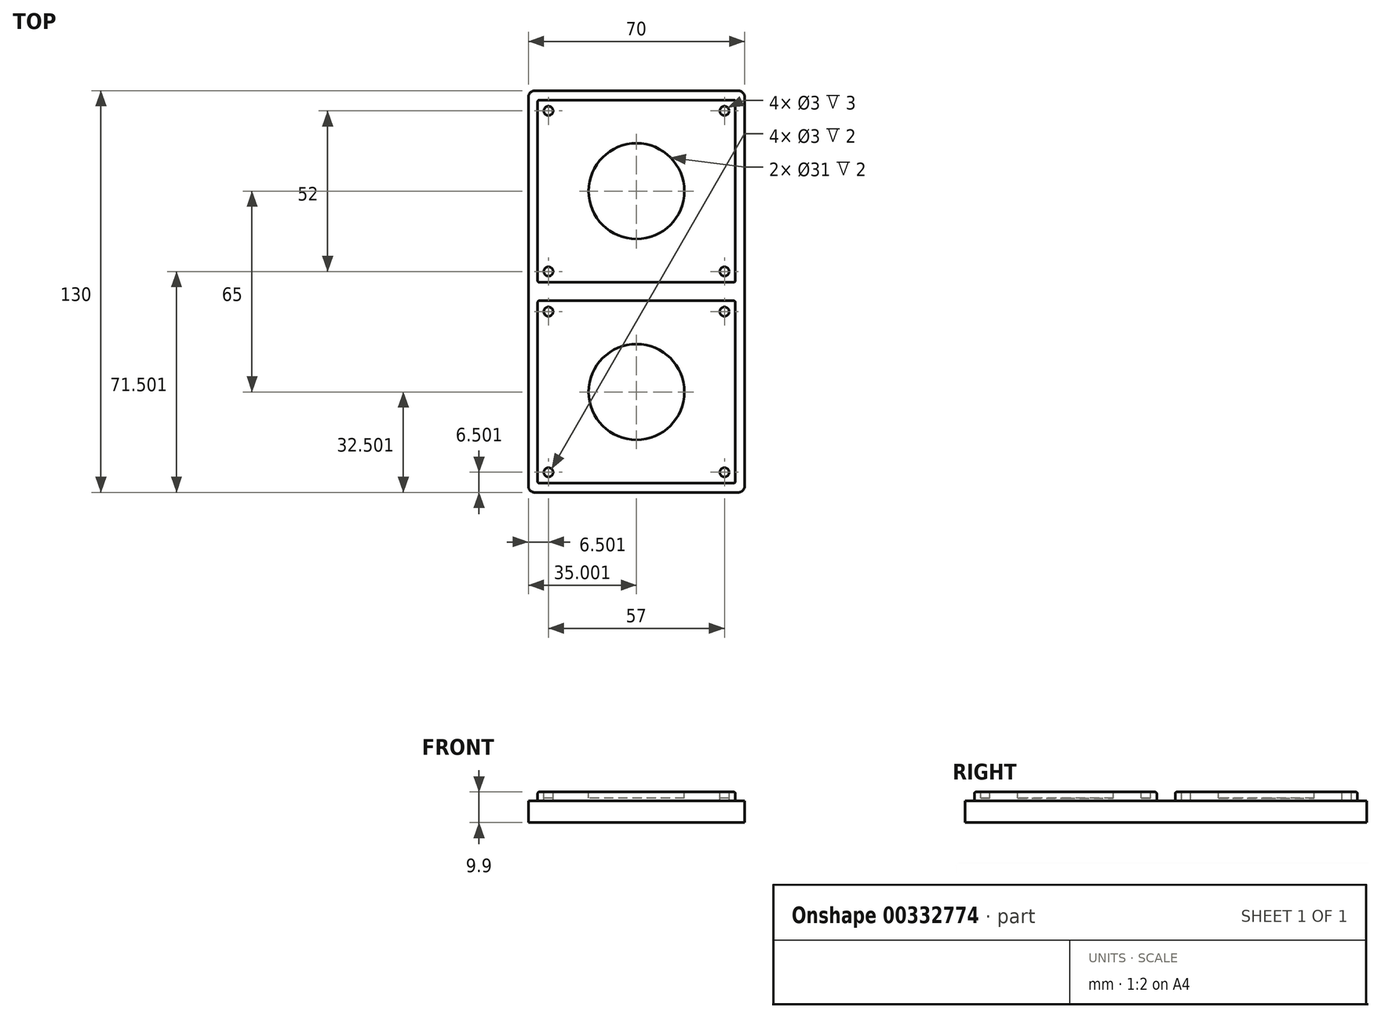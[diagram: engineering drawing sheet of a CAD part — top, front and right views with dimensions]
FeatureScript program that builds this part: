
annotation { "Feature Type Name" : "Feature", "Feature Type Description" : "" }
export const myFeature = defineFeature(function(context is Context, id is Id, definition is map)
    precondition{}
    {
        {
            var Q0;
            Q0=qCreatedBy(makeId("Top.planeOp"),FACE);
            var sketch = newSketch(context, id + "F0", { "sketchPlane" : qUnion([Q0])});
            skLineSegment(sketch, "E0.bottom", {"start": v(-65.64, 99.82) * mm, "end": v(4.36, 99.82) * mm});
            skLineSegment(sketch, "E0.top", {"start": v(-65.64, -30.18) * mm, "end": v(4.36, -30.18) * mm});
            skLineSegment(sketch, "E0.left", {"start": v(-65.64, 99.82) * mm, "end": v(-65.64, -30.18) * mm});
            skLineSegment(sketch, "E0.right", {"start": v(4.36, 99.82) * mm, "end": v(4.36, -30.18) * mm});
            skSolve(sketch);
        }
        {
            var Q0;
            Q0 = qSketchRegion(id + "F0", true);
            extrude(context, id + "F1", {"entities" : qUnion([Q0]), "depth" : 7 * mm});
        }
        {
            var Q0;
            Q0=makeQuery(id+"F1.opExtrude","CAP_FACE",FACE,{"disambiguationData":[OSD([sQuery(id+"F0.wireOp",EDGE,"E0.bottom"),sQuery(id+"F0.wireOp",EDGE,"E0.top"),sQuery(id+"F0.wireOp",EDGE,"E0.left"),sQuery(id+"F0.wireOp",EDGE,"E0.right")])],"isStart":false});
            var sketch = newSketch(context, id + "F2", { "sketchPlane" : qUnion([Q0])});
            skLineSegment(sketch, "E1.bottom", {"start": v(-65.64, 99.82) * mm, "end": v(4.36, 99.82) * mm});
            skLineSegment(sketch, "E1.top", {"start": v(-65.64, 34.82) * mm, "end": v(4.36, 34.82) * mm});
            skLineSegment(sketch, "E1.left", {"start": v(-65.64, 99.82) * mm, "end": v(-65.64, 34.82) * mm});
            skLineSegment(sketch, "E1.right", {"start": v(4.36, 99.82) * mm, "end": v(4.36, 34.82) * mm});
            skSolve(sketch);
        }
        {
            var Q0;
            Q0=makeQuery(id+"F2.imprint","IMPRINT",FACE,{"disambiguationData":[TD([[makeQuery(id+"F2.imprint","IMPRINT",EDGE,{"derivedFrom":sQuery(id+"F2.wireOp",EDGE,"E1.bottom")}),-1.0]])]});
            var sketch = newSketch(context, id + "F3", { "sketchPlane" : qUnion([Q0])});
            skLineSegment(sketch, "E2.0", {"start": v(-62.64, 96.82) * mm, "end": v(-62.64, 37.82) * mm});
            skLineSegment(sketch, "E2.1", {"start": v(1.36, 96.82) * mm, "end": v(-62.64, 96.82) * mm});
            skLineSegment(sketch, "E2.2", {"start": v(1.36, 37.82) * mm, "end": v(1.36, 96.82) * mm});
            skLineSegment(sketch, "E2.3", {"start": v(-62.64, 37.82) * mm, "end": v(1.36, 37.82) * mm});
            skSolve(sketch);
        }
        {
            var Q0;
            {var subQ0=sQuery(id+"F2.wireOp",EDGE,"E1.top");Q0=makeQuery(id+"F2.imprint","IMPRINT",FACE,{"disambiguationData":[TD([[makeQuery(id+"F2.imprint","IMPRINT",EDGE,{"derivedFrom":subQ0}),-1.0]])]});}
            var sketch = newSketch(context, id + "F4", { "sketchPlane" : qUnion([Q0])});
            skLineSegment(sketch, "E3.0", {"start": v(1.36, 31.82) * mm, "end": v(-62.64, 31.82) * mm});
            skLineSegment(sketch, "E3.1", {"start": v(1.36, -27.18) * mm, "end": v(1.36, 31.82) * mm});
            skLineSegment(sketch, "E3.2", {"start": v(-62.64, -27.18) * mm, "end": v(1.36, -27.18) * mm});
            skLineSegment(sketch, "E3.3", {"start": v(-62.64, 31.82) * mm, "end": v(-62.64, -27.18) * mm});
            skSolve(sketch);
        }
        {
            var Q0;
            Q0 = qSketchRegion(id + "F3", true);
            var Q1;
            Q1 = qSketchRegion(id + "F4", true);
            extrude(context, id + "F5", {"entities" : qUnion([Q0, Q1]), "operationType" : NewBodyOperationType.ADD, "depth" : 2.9 * mm});
        }
        {
            var Q0;
            Q0=makeQuery(id+"F5.opExtrude","CAP_FACE",FACE,{"disambiguationData":[OSD([sQuery(id+"F3.wireOp",EDGE,"E2.0"),sQuery(id+"F3.wireOp",EDGE,"E2.1"),sQuery(id+"F3.wireOp",EDGE,"E2.2"),sQuery(id+"F3.wireOp",EDGE,"E2.3")])],"isStart":false});
            var sketch = newSketch(context, id + "F6", { "sketchPlane" : qUnion([Q0])});
            skLineSegment(sketch, "E4.0", {"start": v(-59.14, 93.32) * mm, "end": v(-59.14, 41.32) * mm});
            skLineSegment(sketch, "E4.1", {"start": v(-2.14, 93.32) * mm, "end": v(-59.14, 93.32) * mm});
            skLineSegment(sketch, "E4.2", {"start": v(-2.14, 41.32) * mm, "end": v(-2.14, 93.32) * mm});
            skLineSegment(sketch, "E4.3", {"start": v(-59.14, 41.32) * mm, "end": v(-2.14, 41.32) * mm});
            skCircle(sketch, "E5", {"center": v(-59.14, 93.32) * mm, "radius": 1.5 * mm});
            skCircle(sketch, "E6", {"center": v(-59.14, 41.32) * mm, "radius": 1.5 * mm});
            skCircle(sketch, "E7", {"center": v(-2.14, 93.32) * mm, "radius": 1.5 * mm});
            skCircle(sketch, "E8", {"center": v(-2.14, 41.32) * mm, "radius": 1.5 * mm});
            skSolve(sketch);
        }
        {
            var Q0;
            {var subQ0=sQuery(id+"F6.wireOp",EDGE,"E4.1");var subQ1=sQuery(id+"F6.wireOp",EDGE,"E4.0");var subQ2=makeQuery(id+"F6.imprint","INTERSECT",VERTEX,{"derivedFrom":[subQ1,subQ0]});Q0=makeQuery(id+"F6.imprint","IMPRINT",FACE,{"disambiguationData":[TD([[makeQuery(id+"F6.imprint","IMPRINT",EDGE,{"disambiguationData":[TD([[subQ2,-1.0]])],"derivedFrom":subQ1}),-1.0]])]});}
            var Q1;
            {var subQ0=sQuery(id+"F6.wireOp",EDGE,"E4.1");var subQ1=sQuery(id+"F6.wireOp",EDGE,"E4.0");var subQ2=makeQuery(id+"F6.imprint","INTERSECT",VERTEX,{"derivedFrom":[subQ1,subQ0]});Q1=makeQuery(id+"F6.imprint","IMPRINT",FACE,{"disambiguationData":[TD([[makeQuery(id+"F6.imprint","IMPRINT",EDGE,{"disambiguationData":[TD([[subQ2,-1.0]])],"derivedFrom":subQ1}),1.0]])]});}
            var Q2;
            {var subQ0=sQuery(id+"F6.wireOp",EDGE,"E4.3");var subQ1=sQuery(id+"F6.wireOp",EDGE,"E4.0");var subQ2=makeQuery(id+"F6.imprint","INTERSECT",VERTEX,{"derivedFrom":[subQ1,subQ0]});Q2=makeQuery(id+"F6.imprint","IMPRINT",FACE,{"disambiguationData":[TD([[makeQuery(id+"F6.imprint","IMPRINT",EDGE,{"disambiguationData":[TD([[subQ2,1.0]])],"derivedFrom":subQ1}),-1.0]])]});}
            var Q3;
            {var subQ0=sQuery(id+"F6.wireOp",EDGE,"E4.3");var subQ1=sQuery(id+"F6.wireOp",EDGE,"E4.0");var subQ2=makeQuery(id+"F6.imprint","INTERSECT",VERTEX,{"derivedFrom":[subQ1,subQ0]});Q3=makeQuery(id+"F6.imprint","IMPRINT",FACE,{"disambiguationData":[TD([[makeQuery(id+"F6.imprint","IMPRINT",EDGE,{"disambiguationData":[TD([[subQ2,1.0]])],"derivedFrom":subQ1}),1.0]])]});}
            var Q4;
            {var subQ0=sQuery(id+"F6.wireOp",EDGE,"E4.3");var subQ1=sQuery(id+"F6.wireOp",EDGE,"E4.2");var subQ2=makeQuery(id+"F6.imprint","INTERSECT",VERTEX,{"derivedFrom":[subQ1,subQ0]});Q4=makeQuery(id+"F6.imprint","IMPRINT",FACE,{"disambiguationData":[TD([[makeQuery(id+"F6.imprint","IMPRINT",EDGE,{"disambiguationData":[TD([[subQ2,-1.0]])],"derivedFrom":subQ1}),-1.0]])]});}
            var Q5;
            {var subQ0=sQuery(id+"F6.wireOp",EDGE,"E4.3");var subQ1=sQuery(id+"F6.wireOp",EDGE,"E4.2");var subQ2=makeQuery(id+"F6.imprint","INTERSECT",VERTEX,{"derivedFrom":[subQ1,subQ0]});Q5=makeQuery(id+"F6.imprint","IMPRINT",FACE,{"disambiguationData":[TD([[makeQuery(id+"F6.imprint","IMPRINT",EDGE,{"disambiguationData":[TD([[subQ2,-1.0]])],"derivedFrom":subQ1}),1.0]])]});}
            var Q6;
            {var subQ0=sQuery(id+"F6.wireOp",EDGE,"E4.2");var subQ1=sQuery(id+"F6.wireOp",EDGE,"E4.1");var subQ2=makeQuery(id+"F6.imprint","INTERSECT",VERTEX,{"derivedFrom":[subQ1,subQ0]});Q6=makeQuery(id+"F6.imprint","IMPRINT",FACE,{"disambiguationData":[TD([[makeQuery(id+"F6.imprint","IMPRINT",EDGE,{"disambiguationData":[TD([[subQ2,-1.0]])],"derivedFrom":subQ1}),-1.0]])]});}
            var Q7;
            {var subQ0=sQuery(id+"F6.wireOp",EDGE,"E4.2");var subQ1=sQuery(id+"F6.wireOp",EDGE,"E4.1");var subQ2=makeQuery(id+"F6.imprint","INTERSECT",VERTEX,{"derivedFrom":[subQ1,subQ0]});Q7=makeQuery(id+"F6.imprint","IMPRINT",FACE,{"disambiguationData":[TD([[makeQuery(id+"F6.imprint","IMPRINT",EDGE,{"disambiguationData":[TD([[subQ2,-1.0]])],"derivedFrom":subQ1}),1.0]])]});}
            var Q8;
            Q8=sQuery(id+"F6.wireOp",EDGE,"E5");
            var Q9;
            Q9=sQuery(id+"F6.wireOp",EDGE,"E7");
            var Q10;
            Q10=sQuery(id+"F6.wireOp",EDGE,"E8");
            var Q11;
            Q11=sQuery(id+"F6.wireOp",EDGE,"E6");
            extrude(context, id + "F7", {"entities" : qUnion([Q0, Q1, Q2, Q3, Q4, Q5, Q6, Q7]), "operationType" : NewBodyOperationType.REMOVE, "surfaceEntities" : qUnion([Q8, Q9, Q10, Q11]), "oppositeDirection" : true, "depth" : 3 * mm});
        }
        {
            var Q0;
            Q0=makeQuery(id+"F5.opExtrude","CAP_FACE",FACE,{"disambiguationData":[OSD([sQuery(id+"F4.wireOp",EDGE,"E3.0"),sQuery(id+"F4.wireOp",EDGE,"E3.1"),sQuery(id+"F4.wireOp",EDGE,"E3.2"),sQuery(id+"F4.wireOp",EDGE,"E3.3")])],"isStart":false});
            var sketch = newSketch(context, id + "F8", { "sketchPlane" : qUnion([Q0])});
            skLineSegment(sketch, "E9.0", {"start": v(-2.14, 28.32) * mm, "end": v(-59.14, 28.32) * mm});
            skLineSegment(sketch, "E9.1", {"start": v(-2.14, -23.68) * mm, "end": v(-2.14, 28.32) * mm});
            skLineSegment(sketch, "E9.2", {"start": v(-59.14, -23.68) * mm, "end": v(-2.14, -23.68) * mm});
            skLineSegment(sketch, "E9.3", {"start": v(-59.14, 28.32) * mm, "end": v(-59.14, -23.68) * mm});
            skLineSegment(sketch, "E10.0", {"start": v(6.36, 36.82) * mm, "end": v(-67.64, 36.82) * mm});
            skLineSegment(sketch, "E10.1", {"start": v(6.36, -32.18) * mm, "end": v(6.36, 36.82) * mm});
            skLineSegment(sketch, "E10.2", {"start": v(-67.64, -32.18) * mm, "end": v(6.36, -32.18) * mm});
            skLineSegment(sketch, "E10.3", {"start": v(-67.64, 36.82) * mm, "end": v(-67.64, -32.18) * mm});
            skCircle(sketch, "E11", {"center": v(-59.14, 28.32) * mm, "radius": 1.5 * mm});
            skCircle(sketch, "E12", {"center": v(-59.14, -23.68) * mm, "radius": 1.5 * mm});
            skCircle(sketch, "E13", {"center": v(-2.14, 28.32) * mm, "radius": 1.5 * mm});
            skCircle(sketch, "E14", {"center": v(-2.14, -23.68) * mm, "radius": 1.5 * mm});
            skSolve(sketch);
        }
        {
            var Q0;
            {var subQ0=sQuery(id+"F8.wireOp",EDGE,"E9.3");var subQ1=sQuery(id+"F8.wireOp",EDGE,"E9.0");var subQ2=makeQuery(id+"F8.imprint","INTERSECT",VERTEX,{"derivedFrom":[subQ1,subQ0]});Q0=makeQuery(id+"F8.imprint","IMPRINT",FACE,{"disambiguationData":[TD([[makeQuery(id+"F8.imprint","IMPRINT",EDGE,{"disambiguationData":[TD([[subQ2,1.0]])],"derivedFrom":subQ1}),-1.0]])]});}
            var Q1;
            {var subQ0=sQuery(id+"F8.wireOp",EDGE,"E9.3");var subQ1=sQuery(id+"F8.wireOp",EDGE,"E9.0");var subQ2=makeQuery(id+"F8.imprint","INTERSECT",VERTEX,{"derivedFrom":[subQ1,subQ0]});Q1=makeQuery(id+"F8.imprint","IMPRINT",FACE,{"disambiguationData":[TD([[makeQuery(id+"F8.imprint","IMPRINT",EDGE,{"disambiguationData":[TD([[subQ2,1.0]])],"derivedFrom":subQ1}),1.0]])]});}
            var Q2;
            {var subQ0=sQuery(id+"F8.wireOp",EDGE,"E9.3");var subQ1=sQuery(id+"F8.wireOp",EDGE,"E9.2");var subQ2=makeQuery(id+"F8.imprint","INTERSECT",VERTEX,{"derivedFrom":[subQ1,subQ0]});Q2=makeQuery(id+"F8.imprint","IMPRINT",FACE,{"disambiguationData":[TD([[makeQuery(id+"F8.imprint","IMPRINT",EDGE,{"disambiguationData":[TD([[subQ2,-1.0]])],"derivedFrom":subQ1}),-1.0]])]});}
            var Q3;
            {var subQ0=sQuery(id+"F8.wireOp",EDGE,"E9.3");var subQ1=sQuery(id+"F8.wireOp",EDGE,"E9.2");var subQ2=makeQuery(id+"F8.imprint","INTERSECT",VERTEX,{"derivedFrom":[subQ1,subQ0]});Q3=makeQuery(id+"F8.imprint","IMPRINT",FACE,{"disambiguationData":[TD([[makeQuery(id+"F8.imprint","IMPRINT",EDGE,{"disambiguationData":[TD([[subQ2,-1.0]])],"derivedFrom":subQ1}),1.0]])]});}
            var Q4;
            {var subQ0=sQuery(id+"F8.wireOp",EDGE,"E9.1");var subQ1=sQuery(id+"F8.wireOp",EDGE,"E9.0");var subQ2=makeQuery(id+"F8.imprint","INTERSECT",VERTEX,{"derivedFrom":[subQ1,subQ0]});Q4=makeQuery(id+"F8.imprint","IMPRINT",FACE,{"disambiguationData":[TD([[makeQuery(id+"F8.imprint","IMPRINT",EDGE,{"disambiguationData":[TD([[subQ2,-1.0]])],"derivedFrom":subQ1}),-1.0]])]});}
            var Q5;
            {var subQ0=sQuery(id+"F8.wireOp",EDGE,"E9.1");var subQ1=sQuery(id+"F8.wireOp",EDGE,"E9.0");var subQ2=makeQuery(id+"F8.imprint","INTERSECT",VERTEX,{"derivedFrom":[subQ1,subQ0]});Q5=makeQuery(id+"F8.imprint","IMPRINT",FACE,{"disambiguationData":[TD([[makeQuery(id+"F8.imprint","IMPRINT",EDGE,{"disambiguationData":[TD([[subQ2,-1.0]])],"derivedFrom":subQ1}),1.0]])]});}
            var Q6;
            {var subQ0=sQuery(id+"F8.wireOp",EDGE,"E9.2");var subQ1=sQuery(id+"F8.wireOp",EDGE,"E9.1");var subQ2=makeQuery(id+"F8.imprint","INTERSECT",VERTEX,{"derivedFrom":[subQ1,subQ0]});Q6=makeQuery(id+"F8.imprint","IMPRINT",FACE,{"disambiguationData":[TD([[makeQuery(id+"F8.imprint","IMPRINT",EDGE,{"disambiguationData":[TD([[subQ2,-1.0]])],"derivedFrom":subQ1}),-1.0]])]});}
            var Q7;
            {var subQ0=sQuery(id+"F8.wireOp",EDGE,"E9.2");var subQ1=sQuery(id+"F8.wireOp",EDGE,"E9.1");var subQ2=makeQuery(id+"F8.imprint","INTERSECT",VERTEX,{"derivedFrom":[subQ1,subQ0]});Q7=makeQuery(id+"F8.imprint","IMPRINT",FACE,{"disambiguationData":[TD([[makeQuery(id+"F8.imprint","IMPRINT",EDGE,{"disambiguationData":[TD([[subQ2,-1.0]])],"derivedFrom":subQ1}),1.0]])]});}
            var Q8;
            Q8=sQuery(id+"F8.wireOp",EDGE,"E11");
            var Q9;
            Q9=sQuery(id+"F8.wireOp",EDGE,"E12");
            var Q10;
            Q10=sQuery(id+"F8.wireOp",EDGE,"E14");
            var Q11;
            Q11=sQuery(id+"F8.wireOp",EDGE,"E13");
            extrude(context, id + "F9", {"entities" : qUnion([Q0, Q1, Q2, Q3, Q4, Q5, Q6, Q7]), "operationType" : NewBodyOperationType.REMOVE, "surfaceEntities" : qUnion([Q8, Q9, Q10, Q11]), "oppositeDirection" : true, "depth" : 2 * mm});
        }
        {
            var Q0;
            Q0=makeQuery(id+"F5.opExtrude","CAP_EDGE",EDGE,{"disambiguationData":[OSD([sQuery(id+"F3.wireOp",EDGE,"E2.3")])],"isStart":false});
            var Q1;
            Q1=makeQuery(id+"F5.opExtrude","CAP_EDGE",EDGE,{"disambiguationData":[OSD([sQuery(id+"F3.wireOp",EDGE,"E2.2")])],"isStart":false});
            var Q2;
            Q2=makeQuery(id+"F5.opExtrude","CAP_EDGE",EDGE,{"disambiguationData":[OSD([sQuery(id+"F4.wireOp",EDGE,"E3.1")])],"isStart":false});
            var Q3;
            Q3=makeQuery(id+"F5.opExtrude","CAP_EDGE",EDGE,{"disambiguationData":[OSD([sQuery(id+"F4.wireOp",EDGE,"E3.0")])],"isStart":false});
            var Q4;
            Q4=makeQuery(id+"F5.opExtrude","CAP_EDGE",EDGE,{"disambiguationData":[OSD([sQuery(id+"F3.wireOp",EDGE,"E2.1")])],"isStart":false});
            var Q5;
            Q5=makeQuery(id+"F5.opExtrude","CAP_EDGE",EDGE,{"disambiguationData":[OSD([sQuery(id+"F3.wireOp",EDGE,"E2.0")])],"isStart":false});
            var Q6;
            Q6=makeQuery(id+"F5.opExtrude","CAP_EDGE",EDGE,{"disambiguationData":[OSD([sQuery(id+"F4.wireOp",EDGE,"E3.3")])],"isStart":false});
            var Q7;
            Q7=makeQuery(id+"F5.opExtrude","CAP_EDGE",EDGE,{"disambiguationData":[OSD([sQuery(id+"F4.wireOp",EDGE,"E3.2")])],"isStart":false});
            var Q8;
            Q8=makeQuery(id+"F5.opExtrude","SWEPT_EDGE",EDGE,{"disambiguationData":[OSD([sQuery(id+"F4.wireOp",EDGE,"E3.1"),sQuery(id+"F4.wireOp",EDGE,"E3.2")])]});
            var Q9;
            Q9=makeQuery(id+"F5.opExtrude","SWEPT_EDGE",EDGE,{"disambiguationData":[OSD([sQuery(id+"F4.wireOp",EDGE,"E3.0"),sQuery(id+"F4.wireOp",EDGE,"E3.1")])]});
            var Q10;
            Q10=makeQuery(id+"F5.opExtrude","SWEPT_EDGE",EDGE,{"disambiguationData":[OSD([sQuery(id+"F3.wireOp",EDGE,"E2.2"),sQuery(id+"F3.wireOp",EDGE,"E2.3")])]});
            var Q11;
            Q11=makeQuery(id+"F5.opExtrude","SWEPT_EDGE",EDGE,{"disambiguationData":[OSD([sQuery(id+"F3.wireOp",EDGE,"E2.1"),sQuery(id+"F3.wireOp",EDGE,"E2.2")])]});
            var Q12;
            Q12=makeQuery(id+"F5.opExtrude","SWEPT_EDGE",EDGE,{"disambiguationData":[OSD([sQuery(id+"F4.wireOp",EDGE,"E3.2"),sQuery(id+"F4.wireOp",EDGE,"E3.3")])]});
            var Q13;
            Q13=makeQuery(id+"F5.opExtrude","SWEPT_EDGE",EDGE,{"disambiguationData":[OSD([sQuery(id+"F4.wireOp",EDGE,"E3.0"),sQuery(id+"F4.wireOp",EDGE,"E3.3")])]});
            var Q14;
            Q14=makeQuery(id+"F5.opExtrude","SWEPT_EDGE",EDGE,{"disambiguationData":[OSD([sQuery(id+"F3.wireOp",EDGE,"E2.0"),sQuery(id+"F3.wireOp",EDGE,"E2.3")])]});
            var Q15;
            Q15=makeQuery(id+"F5.opExtrude","SWEPT_EDGE",EDGE,{"disambiguationData":[OSD([sQuery(id+"F3.wireOp",EDGE,"E2.0"),sQuery(id+"F3.wireOp",EDGE,"E2.1")])]});
            fillet(context, id + "F10", {"entities" : qUnion([Q0, Q1, Q2, Q3, Q4, Q5, Q6, Q7, Q8, Q9, Q10, Q11, Q12, Q13, Q14, Q15]), "radius" : 0.5 * mm, "tangentPropagation" : true, "allowEdgeOverflow" : false});
        }
        {
            var Q0;
            Q0=makeQuery(id+"F5.opExtrude","CAP_FACE",FACE,{"disambiguationData":[OSD([sQuery(id+"F4.wireOp",EDGE,"E3.0"),sQuery(id+"F4.wireOp",EDGE,"E3.1"),sQuery(id+"F4.wireOp",EDGE,"E3.2"),sQuery(id+"F4.wireOp",EDGE,"E3.3")])],"isStart":false});
            var sketch = newSketch(context, id + "F11", { "sketchPlane" : qUnion([Q0])});
            skCircle(sketch, "E15", {"center": v(-30.64, 2.32) * mm, "radius": 15.5 * mm});
            skPoint(sketch, "E15.centerSnap0", {"position": v(-30.64, 31.32) * mm});
            skPoint(sketch, "E15.centerSnap1", {"position": v(-62.14, 2.32) * mm});
            skSolve(sketch);
        }
        {
            var Q0;
            Q0=makeQuery(id+"F11.imprint","IMPRINT",FACE,{"disambiguationData":[TD([[makeQuery(id+"F11.imprint","IMPRINT",EDGE,{"derivedFrom":sQuery(id+"F11.wireOp",EDGE,"E15")}),1.0]])]});
            extrude(context, id + "F12", {"entities" : qUnion([Q0]), "operationType" : NewBodyOperationType.REMOVE, "oppositeDirection" : true, "depth" : 2 * mm});
        }
        {
            var Q0;
            Q0=makeQuery(id+"F5.opExtrude","CAP_FACE",FACE,{"disambiguationData":[OSD([sQuery(id+"F3.wireOp",EDGE,"E2.0"),sQuery(id+"F3.wireOp",EDGE,"E2.1"),sQuery(id+"F3.wireOp",EDGE,"E2.2"),sQuery(id+"F3.wireOp",EDGE,"E2.3")])],"isStart":false});
            var sketch = newSketch(context, id + "F13", { "sketchPlane" : qUnion([Q0])});
            skCircle(sketch, "E16", {"center": v(-30.64, 67.32) * mm, "radius": 15.5 * mm});
            skPoint(sketch, "E16.centerSnap0", {"position": v(-30.64, 96.32) * mm});
            skPoint(sketch, "E16.centerSnap1", {"position": v(-62.14, 67.32) * mm});
            skSolve(sketch);
        }
        {
            var Q0;
            Q0 = qSketchRegion(id + "F13", true);
            extrude(context, id + "F14", {"entities" : qUnion([Q0]), "operationType" : NewBodyOperationType.REMOVE, "oppositeDirection" : true, "depth" : 2 * mm});
        }
        {
            var Q0;
            Q0=makeQuery(id+"F1.opExtrude","SWEPT_EDGE",EDGE,{"disambiguationData":[OSD([sQuery(id+"F0.wireOp",EDGE,"E0.top"),sQuery(id+"F0.wireOp",EDGE,"E0.left")])]});
            var Q1;
            Q1=makeQuery(id+"F1.opExtrude","SWEPT_EDGE",EDGE,{"disambiguationData":[OSD([sQuery(id+"F0.wireOp",EDGE,"E0.top"),sQuery(id+"F0.wireOp",EDGE,"E0.right")])]});
            var Q2;
            Q2=makeQuery(id+"F1.opExtrude","SWEPT_EDGE",EDGE,{"disambiguationData":[OSD([sQuery(id+"F0.wireOp",EDGE,"E0.bottom"),sQuery(id+"F0.wireOp",EDGE,"E0.right")])]});
            var Q3;
            Q3=makeQuery(id+"F1.opExtrude","SWEPT_EDGE",EDGE,{"disambiguationData":[OSD([sQuery(id+"F0.wireOp",EDGE,"E0.bottom"),sQuery(id+"F0.wireOp",EDGE,"E0.left")])]});
            fillet(context, id + "F15", {"entities" : qUnion([Q0, Q1, Q2, Q3]), "radius" : 2 * mm, "tangentPropagation" : true, "allowEdgeOverflow" : false});
        }
    });
